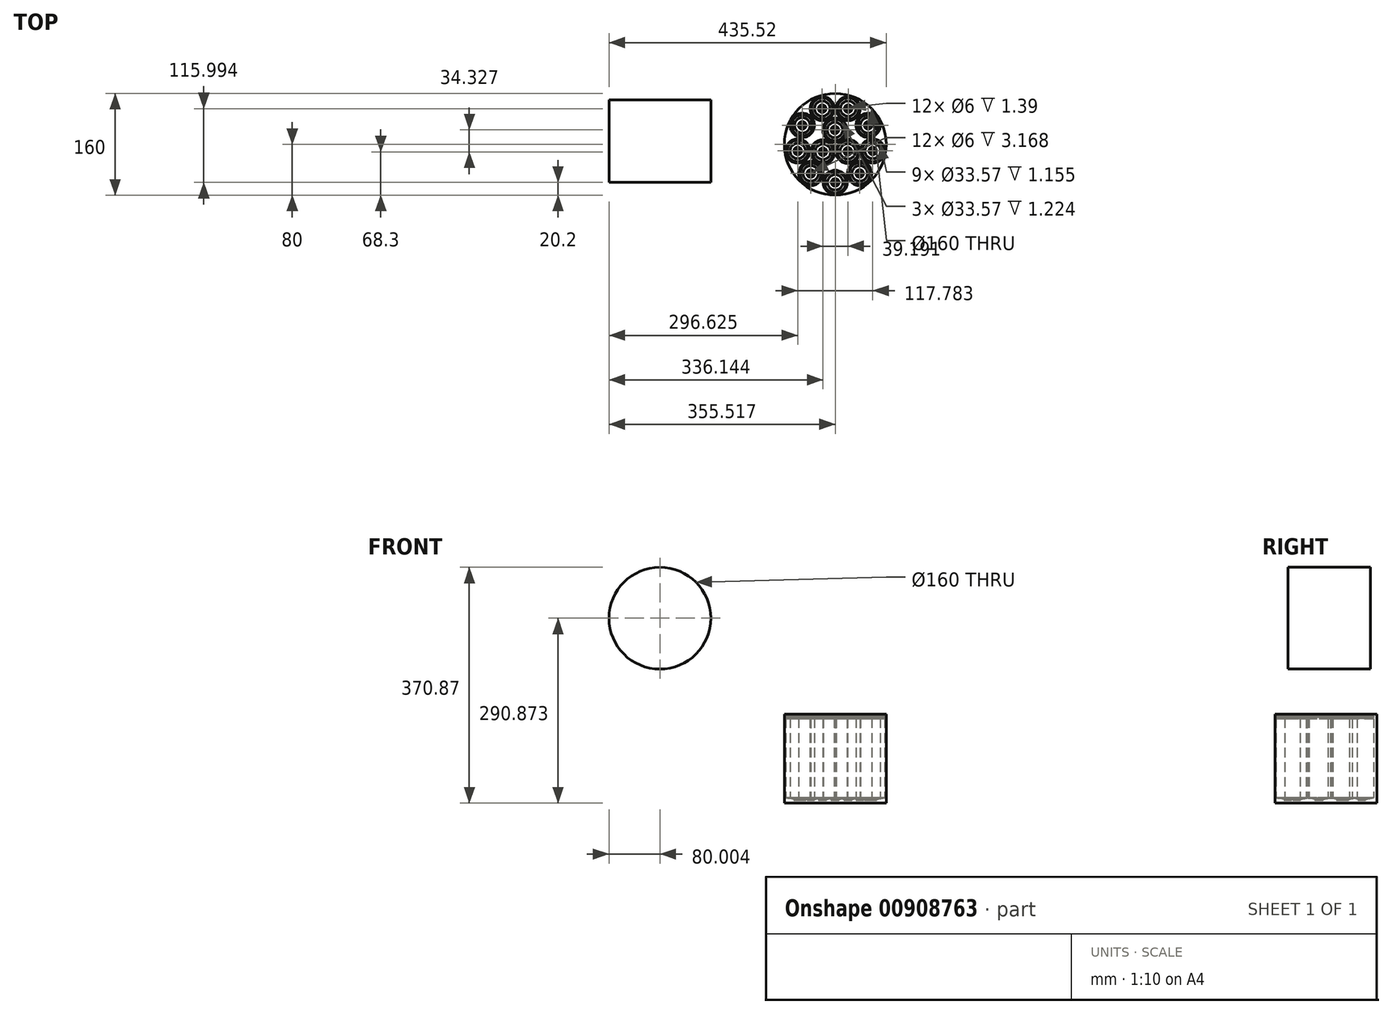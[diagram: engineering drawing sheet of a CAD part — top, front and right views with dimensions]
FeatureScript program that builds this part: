
annotation { "Feature Type Name" : "Feature", "Feature Type Description" : "" }
export const myFeature = defineFeature(function(context is Context, id is Id, definition is map)
    precondition{}
    {
        {
            var Q0;
            Q0=qCreatedBy(makeId("Front.planeOp"),FACE);
            var sketch = newSketch(context, id + "F0", { "sketchPlane" : qUnion([Q0])});
            skCircle(sketch, "E0", {"center": v(-110.44, -11.07) * mm, "radius": 80 * mm});
            skCircle(sketch, "E1", {"center": v(-110.44, -70.87) * mm, "radius": 19 * mm});
            skCircle(sketch, "E2.1.0", {"center": v(-72, -56.88) * mm, "radius": 19 * mm});
            skCircle(sketch, "E2.2.0", {"center": v(-51.54, -21.45) * mm, "radius": 19 * mm});
            skCircle(sketch, "E2.3.0", {"center": v(-58.65, 18.83) * mm, "radius": 19 * mm});
            skCircle(sketch, "E2.4.0", {"center": v(-89.98, 45.13) * mm, "radius": 19 * mm});
            skCircle(sketch, "E2.5.0", {"center": v(-130.89, 45.13) * mm, "radius": 19 * mm});
            skCircle(sketch, "E2.6.0", {"center": v(-162.22, 18.83) * mm, "radius": 19 * mm});
            skCircle(sketch, "E2.7.0", {"center": v(-169.33, -21.45) * mm, "radius": 19 * mm});
            skCircle(sketch, "E2.8.0", {"center": v(-148.88, -56.88) * mm, "radius": 19 * mm});
            skCircle(sketch, "E3", {"center": v(-90.62, -22) * mm, "radius": 19 * mm});
            skCircle(sketch, "E4.1.0", {"center": v(-110.88, 11.56) * mm, "radius": 19 * mm});
            skCircle(sketch, "E4.2.0", {"center": v(-129.8, -22.77) * mm, "radius": 19 * mm});
            skLineSegment(sketch, "E5", {"start": v(162.08, -161.94) * mm, "end": v(159.08, -161.94) * mm});
            skLineSegment(sketch, "E6", {"start": v(159.08, -161.94) * mm, "end": v(159.08, -164.25) * mm});
            skLineSegment(sketch, "E7", {"start": v(159.08, -164.25) * mm, "end": v(152.93, -164.25) * mm});
            skLineSegment(sketch, "E8", {"start": v(152.93, -164.25) * mm, "end": v(152.93, -166.47) * mm});
            skLineSegment(sketch, "E9", {"start": v(152.93, -166.47) * mm, "end": v(148.3, -166.47) * mm});
            skLineSegment(sketch, "E10", {"start": v(148.3, -166.47) * mm, "end": v(148.3, -165.32) * mm});
            skLineSegment(sketch, "E11", {"start": v(148.3, -165.32) * mm, "end": v(146.08, -165.32) * mm});
            skLineSegment(sketch, "E12", {"start": v(146.08, -165.32) * mm, "end": v(146.08, -167.15) * mm});
            skLineSegment(sketch, "E13", {"start": v(146.08, -168.81) * mm, "end": v(146.08, -293.27) * mm});
            skLineSegment(sketch, "E14", {"start": v(146.08, -293.27) * mm, "end": v(149.06, -293.27) * mm});
            skArc(sketch, "E15", {"start": v(146.08, -168.81) * mm, "mid": v(146.91, -167.98) * mm, "end": v(146.08, -167.15) * mm});
            skLineSegment(sketch, "E16", {"start": v(165.08, -135.7) * mm, "end": v(165.08, -317.87) * mm, "construction": true});
            skLineSegment(sketch, "E17", {"start": v(162.08, -161.94) * mm, "end": v(162.08, -163.33) * mm});
            skLineSegment(sketch, "E18", {"start": v(162.08, -163.33) * mm, "end": v(165.08, -163.33) * mm});
            skPoint(sketch, "E19.orphan", {"position": v(165.08, -161.94) * mm});
            skPoint(sketch, "E20.end.orphan", {"position": v(165.08, -317.87) * mm});
            skPoint(sketch, "E21.orphan", {"position": v(165.08, -497.52) * mm});
            skLineSegment(sketch, "E22", {"start": v(149.06, -293.27) * mm, "end": v(149.06, -294.1) * mm});
            skLineSegment(sketch, "E23", {"start": v(149.06, -294.1) * mm, "end": v(159.08, -295.75) * mm});
            skLineSegment(sketch, "E24", {"start": v(159.08, -295.75) * mm, "end": v(159.08, -296.94) * mm});
            skLineSegment(sketch, "E25", {"start": v(159.08, -296.94) * mm, "end": v(162.08, -296.94) * mm});
            skLineSegment(sketch, "E26", {"start": v(162.08, -296.94) * mm, "end": v(162.08, -293.77) * mm});
            skLineSegment(sketch, "E27", {"start": v(162.08, -293.77) * mm, "end": v(165.08, -293.77) * mm});
            skSolve(sketch);
        }
        {
            var Q0;
            Q0=sQuery(id+"F0.wireOp",EDGE,"E13");
            var Q1;
            Q1=sQuery(id+"F0.wireOp",EDGE,"E25");
            var Q2;
            Q2=sQuery(id+"F0.wireOp",EDGE,"E27");
            var Q3;
            Q3=sQuery(id+"F0.wireOp",EDGE,"E23");
            var Q4;
            Q4=sQuery(id+"F0.wireOp",EDGE,"E7");
            var Q5;
            Q5=sQuery(id+"F0.wireOp",EDGE,"E26");
            var Q6;
            Q6=sQuery(id+"F0.wireOp",EDGE,"E18");
            var Q7;
            Q7=sQuery(id+"F0.wireOp",EDGE,"E6");
            var Q8;
            Q8=sQuery(id+"F0.wireOp",EDGE,"E5");
            var Q9;
            Q9=sQuery(id+"F0.wireOp",EDGE,"E8");
            var Q10;
            Q10=sQuery(id+"F0.wireOp",EDGE,"E17");
            var Q11;
            Q11=sQuery(id+"F0.wireOp",EDGE,"E24");
            var Q12;
            Q12=sQuery(id+"F0.wireOp",EDGE,"E14");
            var Q13;
            Q13=sQuery(id+"F0.wireOp",EDGE,"E22");
            var Q14;
            Q14=sQuery(id+"F0.wireOp",EDGE,"E9");
            var Q15;
            Q15=sQuery(id+"F0.wireOp",EDGE,"E10");
            var Q16;
            Q16=sQuery(id+"F0.wireOp",EDGE,"E11");
            var Q17;
            Q17=sQuery(id+"F0.wireOp",EDGE,"E12");
            var Q18;
            Q18=sQuery(id+"F0.wireOp",EDGE,"E15");
            var Q19;
            Q19=sQuery(id+"F0.wireOp",EDGE,"E16");
            revolve(context, id + "F1", {"bodyType" : ToolBodyType.SURFACE, "surfaceOperationType" : NewSurfaceOperationType.NEW, "surfaceEntities" : qUnion([Q0, Q1, Q2, Q3, Q4, Q5, Q6, Q7, Q8, Q9, Q10, Q11, Q12, Q13, Q14, Q15, Q16, Q17, Q18]), "axis" : qUnion([Q19]), "revolveType" : RevolveType.FULL});
        }
        {
            var Q0;
            Q0=makeQuery(id+"F1.opRevolve","SWEPT_FACE",FACE,{"disambiguationData":[OSD([sQuery(id+"F0.wireOp",EDGE,"E5")])]});
            var sketch = newSketch(context, id + "F2", { "sketchPlane" : qUnion([Q0])});
            skCircle(sketch, "E28", {"center": v(165.08, 59.8) * mm, "radius": 2.11 * mm});
            skCircle(sketch, "E29", {"center": v(165.08, 59.8) * mm, "radius": 80 * mm});
            skSolve(sketch);
        }
        {
            var Q0;
            Q0=qCreatedBy(makeId("Front.planeOp"),FACE);
            cPlane(context, id + "F3", {"entities" : qUnion([Q0]), "cplaneType" : CPlaneType.OFFSET, "offset" : 48.87 * mm, "oppositeDirection" : true, "width" : 150 * mm, "height" : 150 * mm});
        }
        {
            var Q0;
            Q0=qCreatedBy(id+"F3.planeOp",FACE);
            var sketch = newSketch(context, id + "F4", { "sketchPlane" : qUnion([Q0])});
            skLineSegment(sketch, "E30", {"start": v(181.9, -162.16) * mm, "end": v(178.9, -162.16) * mm});
            skLineSegment(sketch, "E31", {"start": v(178.9, -162.16) * mm, "end": v(178.9, -164.48) * mm});
            skLineSegment(sketch, "E32", {"start": v(178.9, -164.48) * mm, "end": v(172.75, -164.48) * mm});
            skLineSegment(sketch, "E33", {"start": v(172.75, -164.48) * mm, "end": v(172.75, -166.7) * mm});
            skLineSegment(sketch, "E34", {"start": v(172.75, -166.7) * mm, "end": v(168.11, -166.7) * mm});
            skLineSegment(sketch, "E35", {"start": v(168.11, -166.7) * mm, "end": v(168.11, -165.47) * mm});
            skLineSegment(sketch, "E36", {"start": v(168.11, -165.47) * mm, "end": v(165.9, -165.47) * mm});
            skLineSegment(sketch, "E37", {"start": v(165.9, -165.47) * mm, "end": v(165.9, -167.3) * mm});
            skLineSegment(sketch, "E38", {"start": v(165.9, -168.97) * mm, "end": v(165.9, -293.5) * mm});
            skLineSegment(sketch, "E39", {"start": v(165.9, -293.5) * mm, "end": v(168.88, -293.5) * mm});
            skArc(sketch, "E40", {"start": v(165.9, -168.97) * mm, "mid": v(166.73, -168.13) * mm, "end": v(165.9, -167.3) * mm});
            skLineSegment(sketch, "E41", {"start": v(184.9, -135.85) * mm, "end": v(184.9, -318.02) * mm, "construction": true});
            skLineSegment(sketch, "E42", {"start": v(181.9, -162.16) * mm, "end": v(181.9, -163.55) * mm});
            skLineSegment(sketch, "E43", {"start": v(181.9, -163.55) * mm, "end": v(184.9, -163.55) * mm});
            skPoint(sketch, "E44.orphan", {"position": v(184.9, -162.16) * mm});
            skPoint(sketch, "E45.end.orphan", {"position": v(184.9, -318.02) * mm});
            skLineSegment(sketch, "E46", {"start": v(168.88, -293.5) * mm, "end": v(168.88, -294.33) * mm});
            skLineSegment(sketch, "E47", {"start": v(168.88, -294.33) * mm, "end": v(178.9, -295.97) * mm});
            skLineSegment(sketch, "E48", {"start": v(178.9, -295.97) * mm, "end": v(178.9, -297.16) * mm});
            skLineSegment(sketch, "E49", {"start": v(178.9, -297.16) * mm, "end": v(181.9, -297.16) * mm});
            skLineSegment(sketch, "E50", {"start": v(181.9, -297.16) * mm, "end": v(181.9, -294) * mm});
            skLineSegment(sketch, "E51", {"start": v(181.9, -294) * mm, "end": v(184.9, -294) * mm});
            skSolve(sketch);
        }
        {
            var Q0;
            Q0=sQuery(id+"F4.wireOp",EDGE,"E32");
            var Q1;
            Q1=sQuery(id+"F4.wireOp",EDGE,"E38");
            var Q2;
            Q2=sQuery(id+"F4.wireOp",EDGE,"E47");
            var Q3;
            Q3=sQuery(id+"F4.wireOp",EDGE,"E31");
            var Q4;
            Q4=sQuery(id+"F4.wireOp",EDGE,"E46");
            var Q5;
            Q5=sQuery(id+"F4.wireOp",EDGE,"E51");
            var Q6;
            Q6=sQuery(id+"F4.wireOp",EDGE,"E43");
            var Q7;
            Q7=sQuery(id+"F4.wireOp",EDGE,"E39");
            var Q8;
            Q8=sQuery(id+"F4.wireOp",EDGE,"E33");
            var Q9;
            Q9=sQuery(id+"F4.wireOp",EDGE,"E34");
            var Q10;
            Q10=sQuery(id+"F4.wireOp",EDGE,"E30");
            var Q11;
            Q11=sQuery(id+"F4.wireOp",EDGE,"E42");
            var Q12;
            Q12=sQuery(id+"F4.wireOp",EDGE,"E35");
            var Q13;
            Q13=sQuery(id+"F4.wireOp",EDGE,"E36");
            var Q14;
            Q14=sQuery(id+"F4.wireOp",EDGE,"E48");
            var Q15;
            Q15=sQuery(id+"F4.wireOp",EDGE,"E49");
            var Q16;
            Q16=sQuery(id+"F4.wireOp",EDGE,"E50");
            var Q17;
            Q17=sQuery(id+"F4.wireOp",EDGE,"E37");
            var Q18;
            Q18=sQuery(id+"F4.wireOp",EDGE,"E40");
            var Q19;
            Q19=sQuery(id+"F4.wireOp",EDGE,"E41");
            revolve(context, id + "F5", {"bodyType" : ToolBodyType.SURFACE, "surfaceOperationType" : NewSurfaceOperationType.NEW, "surfaceEntities" : qUnion([Q0, Q1, Q2, Q3, Q4, Q5, Q6, Q7, Q8, Q9, Q10, Q11, Q12, Q13, Q14, Q15, Q16, Q17, Q18]), "axis" : qUnion([Q19]), "revolveType" : RevolveType.FULL});
        }
        {
            var Q0;
            Q0=makeQuery(id+"F1.opRevolve","SWEPT_BODY",BODY,{"disambiguationData":[OSD([sQuery(id+"F0.wireOp",EDGE,"E5")])]});
            var Q1;
            Q1=sQuery(id+"F2.wireOp",EDGE,"E28");
            circularPattern(context, id + "F6", {"entities" : qUnion([Q0]), "axis" : qUnion([Q1]), "angle" : 360 * degree, "instanceCount" : 9, "equalSpace" : true});
        }
        {
            var Q0;
            Q0=makeQuery(id+"F5.opRevolve","SWEPT_BODY",BODY,{"disambiguationData":[OSD([sQuery(id+"F4.wireOp",EDGE,"E30")])]});
            var Q1;
            Q1=sQuery(id+"F2.wireOp",EDGE,"E28");
            circularPattern(context, id + "F7", {"entities" : qUnion([Q0]), "axis" : qUnion([Q1]), "angle" : 360 * degree, "instanceCount" : 3, "equalSpace" : true});
        }
        {
            var Q0;
            Q0=makeQuery(id+"F2.imprint","IMPRINT",FACE,{"disambiguationData":[TD([[makeQuery(id+"F2.imprint","IMPRINT",EDGE,{"derivedFrom":sQuery(id+"F2.wireOp",EDGE,"E28")}),-1.0]])]});
            var Q1;
            Q1=sQuery(id+"F2.wireOp",EDGE,"E29");
            extrude(context, id + "F8", {"entities" : qUnion([Q0]), "bodyType" : ToolBodyType.SURFACE, "surfaceEntities" : qUnion([Q1]), "oppositeDirection" : true, "depth" : 140 * mm, "offsetDistance" : 25 * mm});
        }
        {
            var Q0;
            Q0=sQuery(id+"F0.wireOp",EDGE,"E0");
            extrude(context, id + "F9", {"bodyType" : ToolBodyType.SURFACE, "surfaceEntities" : qUnion([Q0]), "oppositeDirection" : true, "depth" : 130 * mm, "offsetDistance" : 25 * mm});
        }
    });
